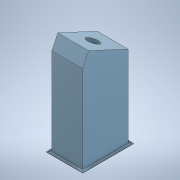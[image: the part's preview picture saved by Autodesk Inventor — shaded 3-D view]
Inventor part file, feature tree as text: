
AUTODESK INVENTOR PART (.ipt)
format: ipt  version: 2022 (Build 260153000, 153)  size: 153,600 bytes
history: native  units: mm
features: extrude x4, sketch x4, chamfer x2, other x1, move_body x1
ambient origin geometry x8: Origin, YZ Plane, XZ Plane, XY Plane, X Axis, Y Axis, Z Axis, Center Point
bodies: SolidBase (feature_tree)
feature tree (12):
  extrude  "Base"  Depth=5.0mm TaperAngle=0.0deg
  extrude  "Stand"  Depth=200.0mm
  other  "Ramp"
  chamfer  "FrontChamfer"  Distance=202.7mm
  chamfer  "BeamHoleFace"  Distance=200.0mm
  extrude  "BeamHole"  [1 undecoded]
  extrude  "BaseBoltHoles"  [1 undecoded]
  sketch  "Sketch1"  dims[d0=5.0mm d1=0.0mm d2=900.0mm d3=0.0mm]
  sketch  "Sketch3"  dims[d23=0.0mm d24=0.0mm d25=200.25mm d26=140.0mm d27=2.0mm d28=4.363323mm d29=202.7mm d30=2.0mm d31=11.34464mm d32=200.0mm d33=0.0mm]
  sketch  "Sketch5"  dims[d34=10.0mm d35=0.0mm]
  sketch  "Sketch6"
  move_body  "Move2"
note: 2 required parameter values undecoded (feature->parameter linkage not recoverable at this tier; creation-order binding heuristic only, values carry confidence <= 0.55)
